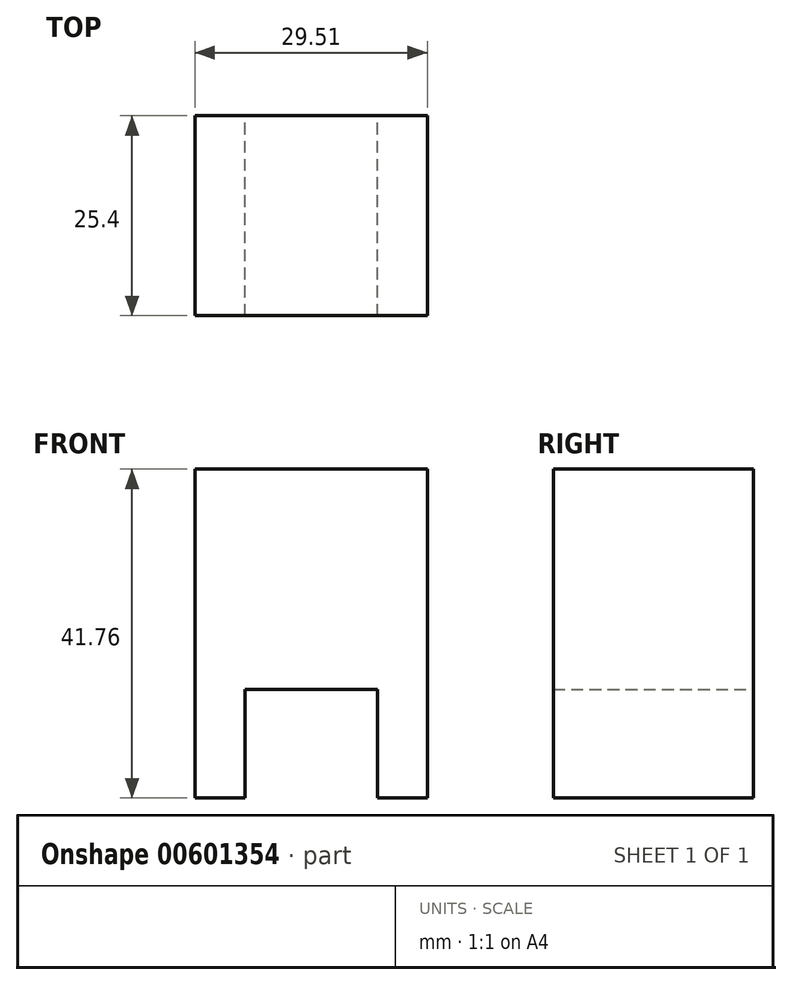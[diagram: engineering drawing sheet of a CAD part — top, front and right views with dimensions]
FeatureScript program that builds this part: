
annotation { "Feature Type Name" : "Feature", "Feature Type Description" : "" }
export const myFeature = defineFeature(function(context is Context, id is Id, definition is map)
    precondition{}
    {
        {
            var Q0;
            Q0=qCreatedBy(makeId("Front.planeOp"),FACE);
            var sketch = newSketch(context, id + "F0", { "sketchPlane" : qUnion([Q0])});
            skLineSegment(sketch, "E0.top", {"start": v(0, 41.76) * mm, "end": v(29.5, 41.76) * mm});
            skLineSegment(sketch, "E0.left", {"start": v(0, 0) * mm, "end": v(0, 41.76) * mm});
            skLineSegment(sketch, "E0.right", {"start": v(29.5, 0) * mm, "end": v(29.5, 41.76) * mm});
            skLineSegment(sketch, "E1", {"start": v(0, 0) * mm, "end": v(6.35, 0) * mm});
            skLineSegment(sketch, "E2", {"start": v(6.35, 0) * mm, "end": v(6.35, 13.8) * mm});
            skLineSegment(sketch, "E3", {"start": v(6.35, 13.8) * mm, "end": v(23.16, 13.8) * mm});
            skLineSegment(sketch, "E4", {"start": v(23.16, 13.8) * mm, "end": v(23.16, 0) * mm});
            skLineSegment(sketch, "E5", {"start": v(23.16, 0) * mm, "end": v(29.5, 0) * mm});
            skSolve(sketch);
        }
        {
            var Q0;
            Q0=makeQuery(id+"F0.imprint","IMPRINT",FACE,{"disambiguationData":[TD([[makeQuery(id+"F0.imprint","IMPRINT",EDGE,{"derivedFrom":sQuery(id+"F0.wireOp",EDGE,"E0.top")}),-1.0]])]});
            extrude(context, id + "F1", {"entities" : qUnion([Q0]), "depth" : 25.4 * mm, "offsetDistance" : 25.4 * mm});
        }
    });
